# Revit family: Vector-IP65-syst-NoHosted-CH-en
name_source: partatom
category: Electrical Equipment
units: mm (PartAtom-declared; Revit-internal decimal feet)

## family parameters
Always vertical = Yes
Cut with Voids When Loaded = No
Panel Configuration = Two Columns, Circuits Across
Part Type = Panelboard
Room Calculation Point = No
Round Connector Dimension = Use Diameter
Shared = No
Work Plane-Based = Yes

## types (21) — shared parameters
Default Elevation = 1219 mm
EF000003 - Mounting method = EV000384 - Surface mounted (plaster)
EF000007 - Colour = EV000270 - Grey
EF000116 - RAL-number = 7035
EF000339 - Type of cover = EV004216 - Door
EF001062 - EMC-version = No
EF001596 - Material housing = EV000139 - Plastic
EF004462 - Type of closure = EV000154 - Other
EF005474 - Degree of protection (IP) = EV006421 - IP65
EF006306 - With lock = No
EF015776 - Earthing terminal block = No
EF015777 - Neutral terminal block = No
EF015941 - Signal passing door = No
HG000001 - Number of columns = 1
HG000002 - With door or cover = Yes
HG000003 - Range = Vector
HG000005 - Thickness = 3 mm  [stored 0.00984252 ft]
HG000006 - Flush mounted = No
HG000009 - Double swing door = No
HG000010 - Asymmetric doors = No
HG000011 - Empty rows from bottom = No
Manufacturer = Hager
Type Comments = Vector
zero-valued in all types: EF000332 - Built-in height, EF000846 - Built-in width, HG000007 - Number of empty columns, HG000008 - Number of empty rows

## per-type parameters (varying)
| type | EF000008 - Width | EF000040 - Height | EF000049 - Depth | EF000118 - With mounting plate | EF000218 - Built-in depth | EF000266 - Number of rows | EF001088 - Extension possible | EF001131 - Internal depth | EF001134 - DIN-rail | EF002950 - Width in number of modular spacings | EF006244 - Transparent cover/door | EF009212 - Cover model | HG000004 - Manufacturer reference | Model |
| Surface mounted IP65 W111 H175 D93 3 Modular spacings - VE103PN | 111 mm | 175 mm  [stored 0.574147 ft] | 93 mm  [stored 0.305118 ft] | No | 0 mm  [stored 0 ft] | 1 | Yes | 93 mm  [stored 0.305118 ft] | Yes | 3 | Yes | EV000116 - Closed | VE103PN | VE103PN |
| Surface mounted IP65 W111 H175 D93 3 Modular spacings - VE103SN | 111 mm | 175 mm  [stored 0.574147 ft] | 93 mm  [stored 0.305118 ft] | No | 0 mm  [stored 0 ft] | 1 | Yes | 93 mm  [stored 0.305118 ft] | Yes | 3 | Yes | EV000116 - Closed | VE103SN | VE103SN |
| Surface mounted IP65 W165 H190 D113 6 Modular spacings - VE106PN | 165 mm | 190 mm | 113 mm  [stored 0.370735 ft] | No | 0 mm  [stored 0 ft] | 1 | Yes | 113 mm  [stored 0.370735 ft] | Yes | 6 | Yes | EV000116 - Closed | VE106PN | VE106PN |
| Surface mounted IP65 W165 H190 D113 6 Modular spacings - VE106SN | 165 mm | 190 mm | 113 mm  [stored 0.370735 ft] | No | 0 mm  [stored 0 ft] | 1 | Yes | 113 mm  [stored 0.370735 ft] | Yes | 6 | Yes | EV000116 - Closed | VE106SN | VE106SN |
| Surface mounted IP65 W237 H210 D114 10 Modular spacings - VE110PN | 237 mm  [stored 0.777559 ft] | 210 mm  [stored 0.688976 ft] | 114 mm  [stored 0.374016 ft] | No | 0 mm  [stored 0 ft] | 1 | Yes | 114 mm  [stored 0.374016 ft] | Yes | 10 | Yes | EV000116 - Closed | VE110PN | VE110PN |
| Surface mounted IP65 W237 H210 D114 10 Modular spacings - VE110SN | 237 mm  [stored 0.777559 ft] | 210 mm  [stored 0.688976 ft] | 114 mm  [stored 0.374016 ft] | No | 0 mm  [stored 0 ft] | 1 | Yes | 114 mm  [stored 0.374016 ft] | Yes | 10 | Yes | EV000116 - Closed | VE110SN | VE110SN |
| Surface mounted IP65 W300 H500 D160 12 Modular spacings - VP36A | 300 mm | 500 mm  [stored 1.64042 ft] | 160 mm  [stored 0.524934 ft] | Yes | 160 mm  [stored 0.524934 ft] | 3 | No | 160 mm  [stored 0.524934 ft] | No | 12 | No | EV009916 - With notch | VP36A | VP36A |
| Surface mounted IP65 W310 H302 D151 12 Modular spacings - VE112PN | 310 mm  [stored 1.01706 ft] | 302 mm  [stored 0.990814 ft] | 151 mm  [stored 0.495407 ft] | No | 0 mm  [stored 0 ft] | 1 | Yes | 151 mm  [stored 0.495407 ft] | Yes | 12 | Yes | EV000116 - Closed | VE112PN | VE112PN |
| Surface mounted IP65 W310 H302 D151 12 Modular spacings - VE112SN | 310 mm  [stored 1.01706 ft] | 302 mm  [stored 0.990814 ft] | 151 mm  [stored 0.495407 ft] | No | 0 mm  [stored 0 ft] | 1 | Yes | 151 mm  [stored 0.495407 ft] | Yes | 12 | Yes | EV000116 - Closed | VE112SN | VE112SN |
| Surface mounted IP65 W310 H427 D151 12 Modular spacings - VE212PN | 310 mm  [stored 1.01706 ft] | 427 mm  [stored 1.40092 ft] | 151 mm  [stored 0.495407 ft] | No | 0 mm  [stored 0 ft] | 2 | Yes | 151 mm  [stored 0.495407 ft] | Yes | 12 | Yes | EV000116 - Closed | VE212PN | VE212PN |
| Surface mounted IP65 W310 H427 D151 12 Modular spacings - VE212SN | 310 mm  [stored 1.01706 ft] | 427 mm  [stored 1.40092 ft] | 151 mm  [stored 0.495407 ft] | No | 0 mm  [stored 0 ft] | 2 | Yes | 151 mm  [stored 0.495407 ft] | Yes | 12 | Yes | EV000116 - Closed | VE212SN | VE212SN |
| Surface mounted IP65 W310 H552 D151 12 Modular spacings - VE312PN | 310 mm  [stored 1.01706 ft] | 552 mm  [stored 1.81102 ft] | 151 mm  [stored 0.495407 ft] | No | 0 mm  [stored 0 ft] | 3 | Yes | 151 mm  [stored 0.495407 ft] | Yes | 12 | Yes | EV000116 - Closed | VE312PN | VE312PN |
| Surface mounted IP65 W310 H552 D151 12 Modular spacings - VE312SN | 310 mm  [stored 1.01706 ft] | 552 mm  [stored 1.81102 ft] | 151 mm  [stored 0.495407 ft] | No | 0 mm  [stored 0 ft] | 3 | Yes | 151 mm  [stored 0.495407 ft] | Yes | 12 | Yes | EV000116 - Closed | VE312SN | VE312SN |
| Surface mounted IP65 W310 H677 D151 12 Modular spacings - VE412PN | 310 mm  [stored 1.01706 ft] | 677 mm  [stored 2.22113 ft] | 151 mm  [stored 0.495407 ft] | No | 0 mm  [stored 0 ft] | 4 | Yes | 151 mm  [stored 0.495407 ft] | Yes | 12 | Yes | EV000116 - Closed | VE412PN | VE412PN |
| Surface mounted IP65 W310 H677 D151 12 Modular spacings - VE412SN | 310 mm  [stored 1.01706 ft] | 677 mm  [stored 2.22113 ft] | 151 mm  [stored 0.495407 ft] | No | 0 mm  [stored 0 ft] | 4 | Yes | 151 mm  [stored 0.495407 ft] | Yes | 12 | Yes | EV000116 - Closed | VE412SN | VE412SN |
| Surface mounted IP65 W418 H302 D151 18 Modular spacings - VE118PN | 418 mm  [stored 1.37139 ft] | 302 mm  [stored 0.990814 ft] | 151 mm  [stored 0.495407 ft] | No | 0 mm  [stored 0 ft] | 1 | Yes | 151 mm  [stored 0.495407 ft] | Yes | 18 | Yes | EV000116 - Closed | VE118PN | VE118PN |
| Surface mounted IP65 W418 H302 D151 18 Modular spacings - VE118SN | 418 mm  [stored 1.37139 ft] | 302 mm  [stored 0.990814 ft] | 151 mm  [stored 0.495407 ft] | No | 0 mm  [stored 0 ft] | 1 | Yes | 151 mm  [stored 0.495407 ft] | Yes | 18 | Yes | EV000116 - Closed | VE118SN | VE118SN |
| Surface mounted IP65 W418 H452 D151 18 Modular spacings - VE218PN | 418 mm  [stored 1.37139 ft] | 452 mm  [stored 1.48294 ft] | 151 mm  [stored 0.495407 ft] | No | 0 mm  [stored 0 ft] | 2 | Yes | 151 mm  [stored 0.495407 ft] | Yes | 18 | Yes | EV000116 - Closed | VE218PN | VE218PN |
| Surface mounted IP65 W418 H452 D151 18 Modular spacings - VE218SN | 418 mm  [stored 1.37139 ft] | 452 mm  [stored 1.48294 ft] | 151 mm  [stored 0.495407 ft] | No | 0 mm  [stored 0 ft] | 2 | Yes | 151 mm  [stored 0.495407 ft] | Yes | 18 | Yes | EV000116 - Closed | VE218SN | VE218SN |
| Surface mounted IP65 W418 H602 D151 18 Modular spacings - VE318PN | 418 mm  [stored 1.37139 ft] | 602 mm  [stored 1.97507 ft] | 151 mm  [stored 0.495407 ft] | No | 0 mm  [stored 0 ft] | 3 | Yes | 151 mm  [stored 0.495407 ft] | Yes | 18 | Yes | EV000116 - Closed | VE318PN | VE318PN |
| Surface mounted IP65 W418 H602 D151 18 Modular spacings - VE318SN | 418 mm  [stored 1.37139 ft] | 602 mm  [stored 1.97507 ft] | 151 mm  [stored 0.495407 ft] | No | 0 mm  [stored 0 ft] | 3 | Yes | 151 mm  [stored 0.495407 ft] | Yes | 18 | Yes | EV000116 - Closed | VE318SN | VE318SN |

note: [stored X ft] marks values corroborated as IEEE doubles in the binary element streams (Revit-internal decimal feet)

## geometry (parser evidence)
native form markers: Sweep x16
no freeform markers — native parametric forms only
